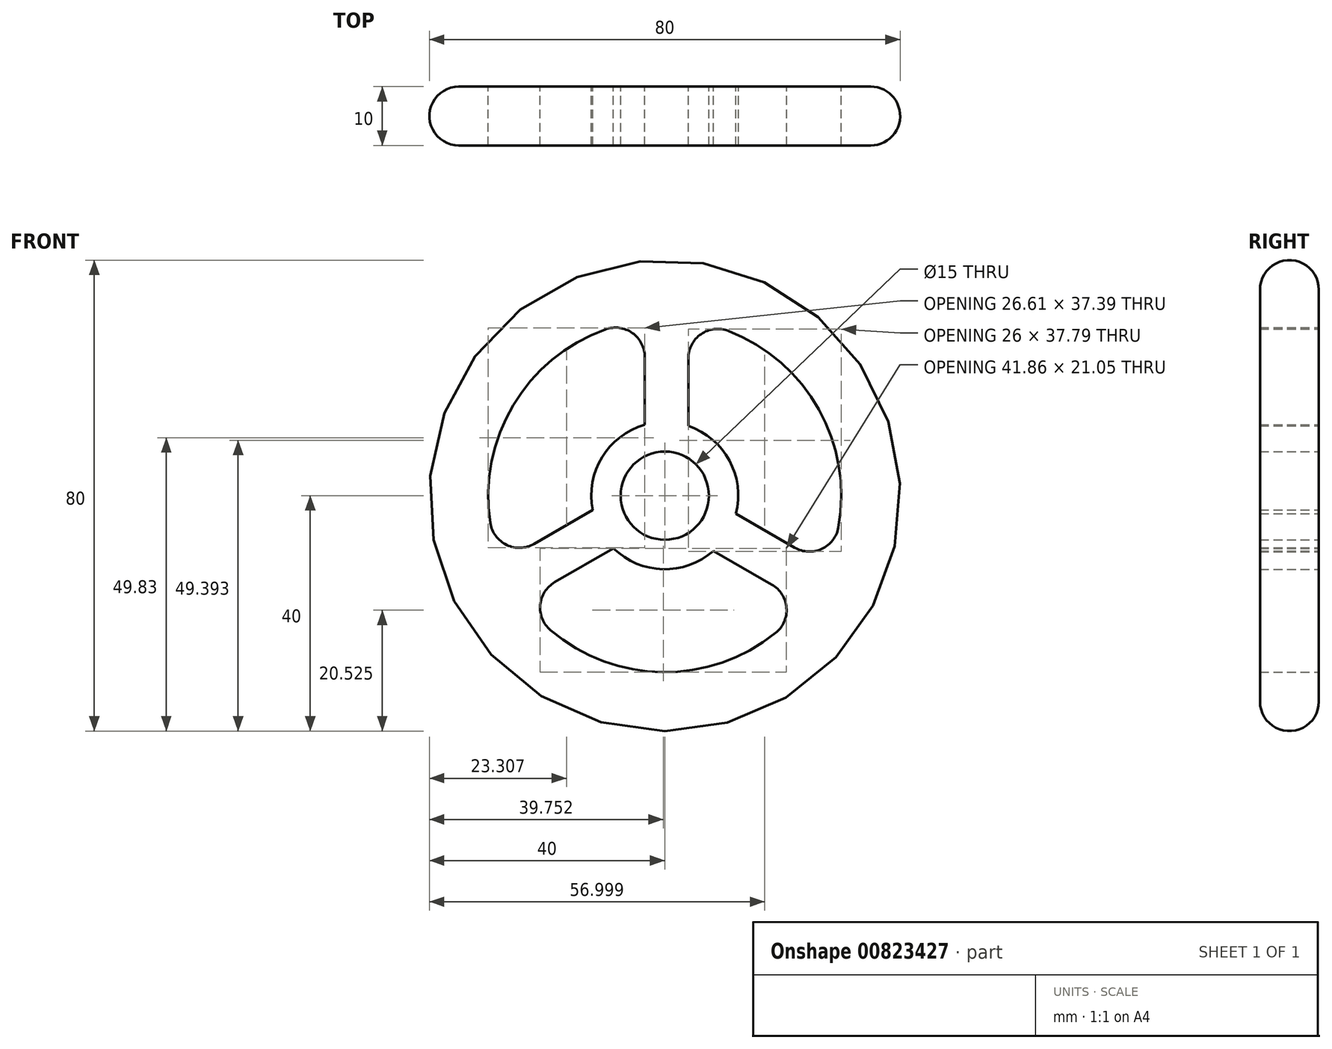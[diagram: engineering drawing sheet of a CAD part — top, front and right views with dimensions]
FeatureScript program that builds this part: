
annotation { "Feature Type Name" : "Feature", "Feature Type Description" : "" }
export const myFeature = defineFeature(function(context is Context, id is Id, definition is map)
    precondition{}
    {
        {
            var Q0;
            Q0=qCreatedBy(makeId("Front.planeOp"),FACE);
            var sketch = newSketch(context, id + "F0", { "sketchPlane" : qUnion([Q0])});
            skCircle(sketch, "E0", {"center": v(0, 0) * mm, "radius": 40 * mm});
            skArc(sketch, "E1", {"start": v(-10.07, 28.26) * mm, "mid": v(-25.78, 15.34) * mm, "end": v(-29.64, -4.64) * mm});
            skCircle(sketch, "E2", {"center": v(0, 0) * mm, "radius": 12.5 * mm});
            skCircle(sketch, "E3", {"center": v(0, 0) * mm, "radius": 7.5 * mm});
            skLineSegment(sketch, "E4.0", {"start": v(-3.4, 40) * mm, "end": v(-3.4, 39.86) * mm});
            skLineSegment(sketch, "E5.0", {"start": v(4, 40) * mm, "end": v(4, 39.8) * mm});
            skLineSegment(sketch, "E6.trimOffspring", {"start": v(-3.4, 23.55) * mm, "end": v(-3.4, 12.03) * mm});
            skLineSegment(sketch, "E7.trimOffspring", {"start": v(4, 23.32) * mm, "end": v(4, 11.84) * mm});
            skPoint(sketch, "E8.orphan", {"position": v(0, 40) * mm});
            skLineSegment(sketch, "E9.1.0", {"start": v(-22.2, -8.2) * mm, "end": v(-12.26, -2.46) * mm});
            skLineSegment(sketch, "E9.1.1", {"start": v(-18.7, -14.71) * mm, "end": v(-8.72, -8.95) * mm});
            skLineSegment(sketch, "E9.2.0", {"start": v(18.2, -15.13) * mm, "end": v(8.26, -9.39) * mm});
            skLineSegment(sketch, "E9.2.1", {"start": v(22.1, -8.84) * mm, "end": v(12.11, -3.08) * mm});
            skArc(sketch, "E10.trimOffspring", {"start": v(-19.44, -22.85) * mm, "mid": v(-0.4, -30) * mm, "end": v(18.84, -23.35) * mm});
            skArc(sketch, "E11.trimOffspring", {"start": v(29.5, -5.41) * mm, "mid": v(26.17, 14.66) * mm, "end": v(10.8, 27.99) * mm});
            skPoint(sketch, "E12.visualSharp", {"position": v(-3.4, 29.8) * mm});
            skArc(sketch, "E12.filletArc", {"start": v(-3.4, 23.55) * mm, "mid": v(-5.5, 27.64) * mm, "end": v(-10.07, 28.26) * mm});
            skPoint(sketch, "E13.visualSharp", {"position": v(4, 29.73) * mm});
            skArc(sketch, "E13.filletArc", {"start": v(10.8, 27.99) * mm, "mid": v(6.17, 27.45) * mm, "end": v(4, 23.32) * mm});
            skPoint(sketch, "E14.visualSharp", {"position": v(27.5, -11.97) * mm});
            skArc(sketch, "E14.filletArc", {"start": v(22.1, -8.84) * mm, "mid": v(26.69, -9.05) * mm, "end": v(29.5, -5.41) * mm});
            skPoint(sketch, "E15.visualSharp", {"position": v(23.75, -18.33) * mm});
            skArc(sketch, "E15.filletArc", {"start": v(18.84, -23.35) * mm, "mid": v(20.68, -19.07) * mm, "end": v(18.2, -15.13) * mm});
            skPoint(sketch, "E16.visualSharp", {"position": v(-24.12, -17.84) * mm});
            skArc(sketch, "E16.filletArc", {"start": v(-18.7, -14.71) * mm, "mid": v(-21.18, -18.59) * mm, "end": v(-19.44, -22.85) * mm});
            skPoint(sketch, "E17.visualSharp", {"position": v(-27.75, -11.4) * mm});
            skArc(sketch, "E17.filletArc", {"start": v(-29.64, -4.64) * mm, "mid": v(-26.86, -8.38) * mm, "end": v(-22.2, -8.2) * mm});
            skSolve(sketch);
        }
        {
            var Q0;
            Q0=qSketchRegion(id+"F0",true);
            var Q1;
            Q1=makeQuery(id+"F0.imprint","IMPRINT",FACE,{"disambiguationData":[TD([[makeQuery(id+"F0.imprint","IMPRINT",EDGE,{"derivedFrom":sQuery(id+"F0.wireOp",EDGE,"E3")}),-1.0]])]});
            extrude(context, id + "F1", {"entities" : qUnion([Q0, Q1]), "depth" : 10 * mm, "offsetDistance" : 25 * mm});
        }
        {
            var Q0;
            Q0=makeQuery(id+"F1.opExtrude","CAP_EDGE",EDGE,{"disambiguationData":[OSD([sQuery(id+"F0.wireOp",EDGE,"E0")])],"isStart":false});
            var Q1;
            Q1=makeQuery(id+"F1.opExtrude","CAP_EDGE",EDGE,{"disambiguationData":[OSD([sQuery(id+"F0.wireOp",EDGE,"E0")])],"isStart":true});
            fillet(context, id + "F2", {"entities" : qUnion([Q0, Q1]), "radius" : 5 * mm, "tangentPropagation" : true, "allowEdgeOverflow" : false});
        }
    });
